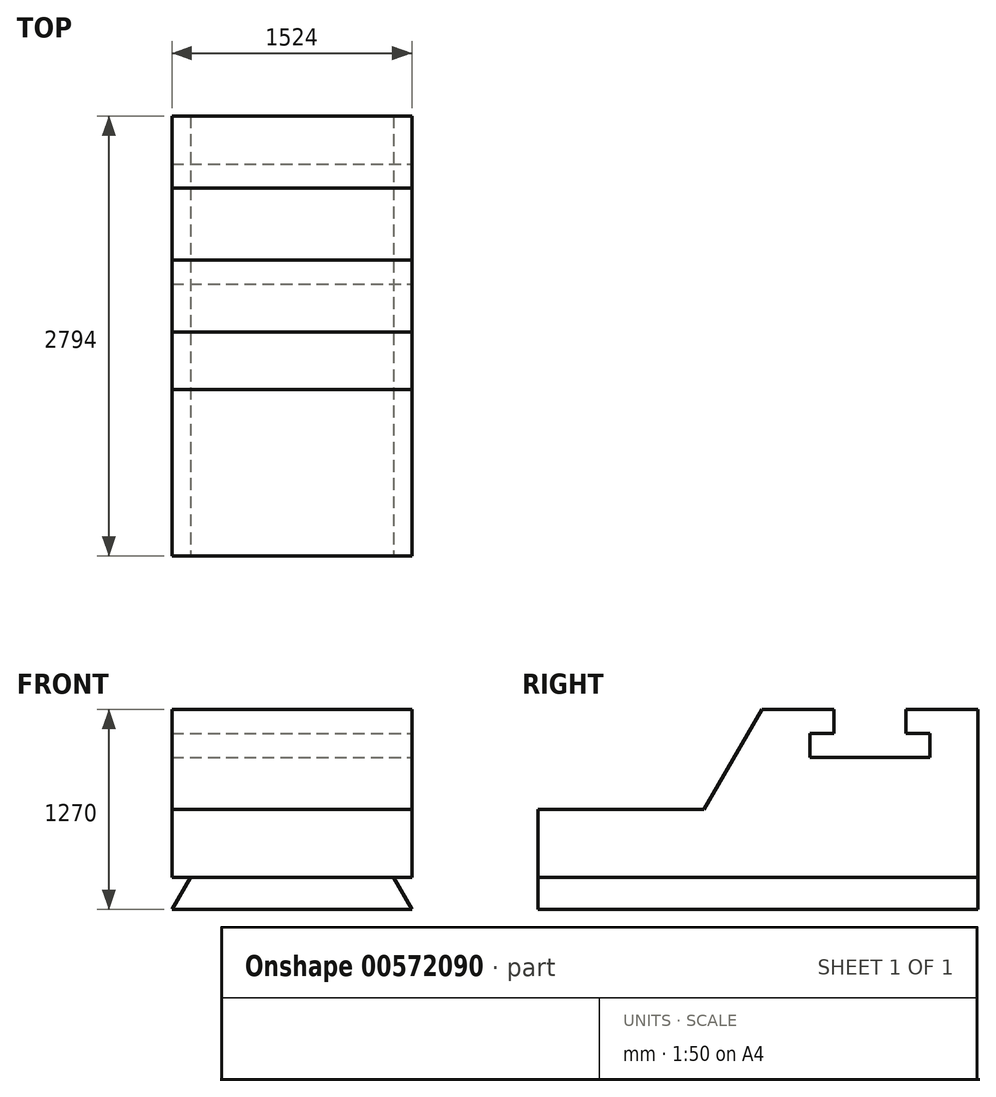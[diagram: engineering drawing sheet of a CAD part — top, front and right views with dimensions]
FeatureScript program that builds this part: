
annotation { "Feature Type Name" : "Feature", "Feature Type Description" : "" }
export const myFeature = defineFeature(function(context is Context, id is Id, definition is map)
    precondition{}
    {
        {
            var Q0;
            Q0=qCreatedBy(makeId("Right.planeOp"),FACE);
            var sketch = newSketch(context, id + "F0", { "sketchPlane" : qUnion([Q0])});
            skLineSegment(sketch, "E0", {"start": v(-1452.43, -69.73) * mm, "end": v(1341.57, -69.73) * mm});
            skLineSegment(sketch, "E1", {"start": v(1341.57, -69.73) * mm, "end": v(1341.57, 1200.27) * mm});
            skLineSegment(sketch, "E2", {"start": v(-1452.43, -69.73) * mm, "end": v(-1452.43, 565.27) * mm});
            skLineSegment(sketch, "E3", {"start": v(-30.03, 1200.27) * mm, "end": v(-396.65, 565.27) * mm});
            skLineSegment(sketch, "E4", {"start": v(-396.65, 565.27) * mm, "end": v(-1452.43, 565.27) * mm});
            skLineSegment(sketch, "E5", {"start": v(1341.57, 1200.27) * mm, "end": v(884.37, 1200.27) * mm});
            skLineSegment(sketch, "E6", {"start": v(884.37, 1200.27) * mm, "end": v(884.37, 1047.87) * mm});
            skLineSegment(sketch, "E7", {"start": v(884.37, 1047.87) * mm, "end": v(1036.77, 1047.87) * mm});
            skLineSegment(sketch, "E8", {"start": v(1036.77, 1047.87) * mm, "end": v(1036.77, 895.47) * mm});
            skLineSegment(sketch, "E9", {"start": v(1036.77, 895.47) * mm, "end": v(274.77, 895.47) * mm});
            skLineSegment(sketch, "E10", {"start": v(274.77, 895.47) * mm, "end": v(274.77, 1047.87) * mm});
            skLineSegment(sketch, "E11", {"start": v(274.77, 1047.87) * mm, "end": v(427.17, 1047.87) * mm});
            skLineSegment(sketch, "E12", {"start": v(427.17, 1047.87) * mm, "end": v(427.17, 1200.27) * mm});
            skLineSegment(sketch, "E13", {"start": v(-30.03, 1200.27) * mm, "end": v(427.17, 1200.27) * mm});
            skLineSegment(sketch, "E14", {"start": v(-1452.43, -69.73) * mm, "end": v(-1452.43, 133.47) * mm});
            skLineSegment(sketch, "E15", {"start": v(-1452.43, 133.47) * mm, "end": v(1341.57, 133.47) * mm});
            skSolve(sketch);
        }
        {
            var Q0;
            Q0=makeQuery(id+"F0.imprint","IMPRINT",FACE,{"disambiguationData":[TD([[makeQuery(id+"F0.imprint","IMPRINT",EDGE,{"derivedFrom":sQuery(id+"F0.wireOp",EDGE,"E3")}),1.0]])]});
            extrude(context, id + "F1", {"entities" : qUnion([Q0]), "oppositeDirection" : true, "depth" : 1524 * mm, "offsetDistance" : 25.4 * mm});
        }
        {
            var Q0;
            {var subQ0=sQuery(id+"F0.wireOp",EDGE,"E0");Q0=makeQuery(id+"F0.imprint","IMPRINT",FACE,{"disambiguationData":[TD([[makeQuery(id+"F0.imprint","IMPRINT",EDGE,{"derivedFrom":subQ0}),1.0]])]});}
            extrude(context, id + "F2", {"entities" : qUnion([Q0]), "oppositeDirection" : true, "depth" : 1524 * mm, "offsetDistance" : 25.4 * mm});
        }
        {
            var Q0;
            Q0=makeQuery(id+"F2.opExtrude","SWEPT_FACE",FACE,{"disambiguationData":[OSD([sQuery(id+"F0.wireOp",EDGE,"E2")])]});
            var sketch = newSketch(context, id + "F3", { "sketchPlane" : qUnion([Q0])});
            skLineSegment(sketch, "E16", {"start": v(0, -69.73) * mm, "end": v(-117.32, 133.47) * mm});
            skLineSegment(sketch, "E17", {"start": v(-1524, -69.73) * mm, "end": v(-1406.68, 133.47) * mm});
            skSolve(sketch);
        }
        {
            var Q0;
            {var subQ0=sQuery(id+"F3.wireOp",EDGE,"E17");Q0=makeQuery(id+"F3.imprint","IMPRINT",FACE,{"disambiguationData":[TD([[makeQuery(id+"F3.imprint","IMPRINT",EDGE,{"derivedFrom":subQ0}),1.0]])]});}
            extrude(context, id + "F4", {"entities" : qUnion([Q0]), "operationType" : NewBodyOperationType.REMOVE, "endBound" : BoundingType.THROUGH_ALL, "oppositeDirection" : true, "depth" : 25.4 * mm, "offsetDistance" : 25.4 * mm});
        }
        {
            var Q0;
            {var subQ0=sQuery(id+"F3.wireOp",EDGE,"E16");Q0=makeQuery(id+"F3.imprint","IMPRINT",FACE,{"disambiguationData":[TD([[makeQuery(id+"F3.imprint","IMPRINT",EDGE,{"derivedFrom":subQ0}),-1.0]])]});}
            extrude(context, id + "F5", {"entities" : qUnion([Q0]), "operationType" : NewBodyOperationType.REMOVE, "endBound" : BoundingType.THROUGH_ALL, "oppositeDirection" : true, "depth" : 25.4 * mm, "offsetDistance" : 25.4 * mm});
        }
    });
